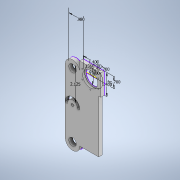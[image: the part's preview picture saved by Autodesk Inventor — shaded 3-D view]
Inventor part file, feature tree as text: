
AUTODESK INVENTOR PART (.ipt)
format: ipt  version: 2021 (Build 250183000, 183)  size: 179,200 bytes
history: native  units: in
note: dims shown in document units (in); Inventor stores cm internally (conversion verified against a paired STEP export)
features: extrude x5, sketch x4, hole x3, projected_geometry x2
ambient origin geometry x8: Origin, YZ Plane, XZ Plane, XY Plane, X Axis, Y Axis, Z Axis, Center Point
bodies: Solid1 (feature_tree)
feature tree (14):
  extrude  "Extrusion1"  Depth=0.98in
  hole  "Hole1"  [1 undecoded]
  hole  "Hole2"  [1 undecoded]
  extrude  "Extrusion2"  TaperAngle=0.0deg  [1 undecoded]
  extrude  "Extrusion3"  Depth=0.25in TaperAngle=0.0deg
  sketch  "Sketch5"  dims[d11=0.2in d12=0.172in d13=0.375in d14=0.25in d15=0.5635in d16=0.2275in d17=0.8108in d18=0.08in d19=0.3937in d20=0.0in d21=0.0in d22=1.25in d23=0.0in d24=1.4in d25=1.4in d26=1.0in d27=0.7in d28=0.7in d29=0.613in d30=2.3622in d32=360.0deg d34=1.25in d35=0.0in d36=0.0in d37=0.0in d38=0.092in d39=0.172in d40=0.375in d41=0.25in d42=0.5635in d43=0.2275in d44=0.8108in]
  extrude  "Extrusion4"  Depth=1.4in
  extrude  "Extrusion5"  Depth=1.4in
  hole  "Hole3"  [1 undecoded]
  sketch  "Sketch2"  dims[d0=2.125in d1=0.98in]
  projected_geometry  "Projected Loop1"
  sketch  "Sketch3"  dims[d2=0.24in d3=0.0in]
  sketch  "Sketch4"  dims[d4=0.5in d5=0.172in d6=0.375in d7=0.25in d8=0.5635in d9=0.2275in d10=0.8108in]
  projected_geometry  "Projected Loop2"
note: 4 required parameter values undecoded (feature->parameter linkage not recoverable at this tier; creation-order binding heuristic only, values carry confidence <= 0.55)
